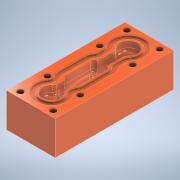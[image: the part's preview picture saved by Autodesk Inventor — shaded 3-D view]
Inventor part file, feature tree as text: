
AUTODESK INVENTOR PART (.ipt)
format: ipt  version: 2021 (Build 250183000, 183)  size: 749,568 bytes
history: native  units: mm
features: projected_geometry x11, extrude x8, sketch x7, fillet x6, hole x3, plane x2
ambient origin geometry x8: Origin, YZ Plane, XZ Plane, XY Plane, X Axis, Y Axis, Z Axis, Center Point
bodies: Solid1 (feature_tree)
feature tree (37):
  extrude  "Extrusion1"  Depth=67.75mm
  hole  "Hole1"  [1 undecoded]
  hole  "Hole2"  [1 undecoded]
  fillet  "Fillet16"  Radius=15.5mm
  extrude  "Extrusion10"  Depth=2.0mm
  fillet  "Fillet15"  Radius=7.0mm
  extrude  "Extrusion2"  Depth=19.5mm
  extrude  "Extrusion5"  TaperAngle=0.0deg  [1 undecoded]
  extrude  "Extrusion11"  Depth=1.0mm
  fillet  "Fillet17"  Radius=5.5mm
  fillet  "Fillet18"  Radius=9.5mm
  fillet  "Fillet19"  Radius=1.0mm
  fillet  "Fillet8"  Radius=1.0mm
  extrude  "Extrusion6"  Depth=1.0mm
  plane  "Work Plane3"
  plane  "Work Plane1"
  extrude  "Extrusion8"  Depth=1.2mm TaperAngle=0.0deg
  hole  "Hole3"  [1 undecoded]
  extrude  "Extrusion12"  Depth=1.2mm TaperAngle=0.0deg
  sketch  "Sketch1"  dims[d0=27.8mm d1=67.75mm]
  sketch  "Sketch2"  dims[d2=19.5mm d3=0.0mm d4=18.8mm]
  projected_geometry  "Projected Loop1"
  sketch  "Sketch3"  dims[d5=30.0mm d6=15.5mm d7=15.5mm]
  projected_geometry  "Projected Loop2"
  projected_geometry  "Projected Loop7"
  projected_geometry  "Projected Loop8"
  sketch  "Sketch12"  dims[d8=3.4mm d9=6.0mm d10=6.3mm d11=2.0mm d12=90.0deg d13=5.0mm d14=0.0mm d15=44.0mm]
  projected_geometry  "Projected Loop11"
  projected_geometry  "Projected Loop14"
  sketch  "Sketch19"  dims[d16=10.8mm d17=6.0mm d18=6.3mm d19=2.0mm d20=90.0deg d21=5.6mm d22=0.0mm d23=7.0mm]
  sketch  "Sketch20"  dims[d24=16.0mm d25=19.5mm]
  projected_geometry  "Projected Loop17"
  projected_geometry  "Projected Loop18"
  projected_geometry  "Projected Loop19"
  projected_geometry  "Projected Loop20"
  sketch  "Sketch21"  dims[d26=2.0mm d27=0.0mm d28=0.0mm d39=4.0mm d42=5.5mm d43=9.5mm d44=0.0mm d51=1.0mm d52=1.0mm d54=4.0mm d56=1.2mm d57=0.0mm d72=1.0mm d74=1.2mm d75=0.0mm d84=3.0mm d85=2.6mm d92=7.5mm d93=7.5mm d94=4.2mm d95=4.2mm d96=4.2mm d97=4.2mm d98=12.15mm d99=4.0mm d100=6.0mm d101=4.0mm d102=2.0mm d103=90.0deg d104=5.4mm d105=20.594885mm d108=1.0mm d109=2.6mm d111=12.0mm d112=12.0mm d113=17.15mm d114=5.5mm d115=2.0mm d116=8.3mm d128=9.4mm d129=19.2mm d130=2.0mm d131=6.4mm d132=0.0mm d133=2.0mm d134=2.0mm d135=5.6mm d136=0.0mm d137=2.0mm d138=2.0mm d139=4.0mm d141=8.0mm d142=1.2mm d143=0.0mm d144=1.0mm]
  projected_geometry  "Projected Loop21"
note: 4 required parameter values undecoded (feature->parameter linkage not recoverable at this tier; creation-order binding heuristic only, values carry confidence <= 0.55)
